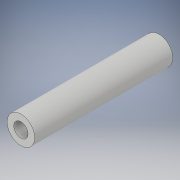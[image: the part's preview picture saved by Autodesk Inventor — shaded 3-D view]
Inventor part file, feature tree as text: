
AUTODESK INVENTOR PART (.ipt)
format: ipt  version: 2017 (Build 210142000, 142)  size: 91,648 bytes
history: native  units: in
note: dims shown in document units (in); Inventor stores cm internally (conversion verified against a paired STEP export)
features: extrude x1, sketch x1
ambient origin geometry x8: Origin, YZ Plane, XZ Plane, XY Plane, X Axis, Y Axis, Z Axis, Center Point
bodies: Solid1 (feature_tree)
feature tree (2):
  extrude  "Extrusion1"  [1 undecoded]
  sketch  "Sketch1"  dims[d0=2.5in d1=0.0in]
note: 1 required parameter value undecoded (feature->parameter linkage not recoverable at this tier; creation-order binding heuristic only, values carry confidence <= 0.55)
